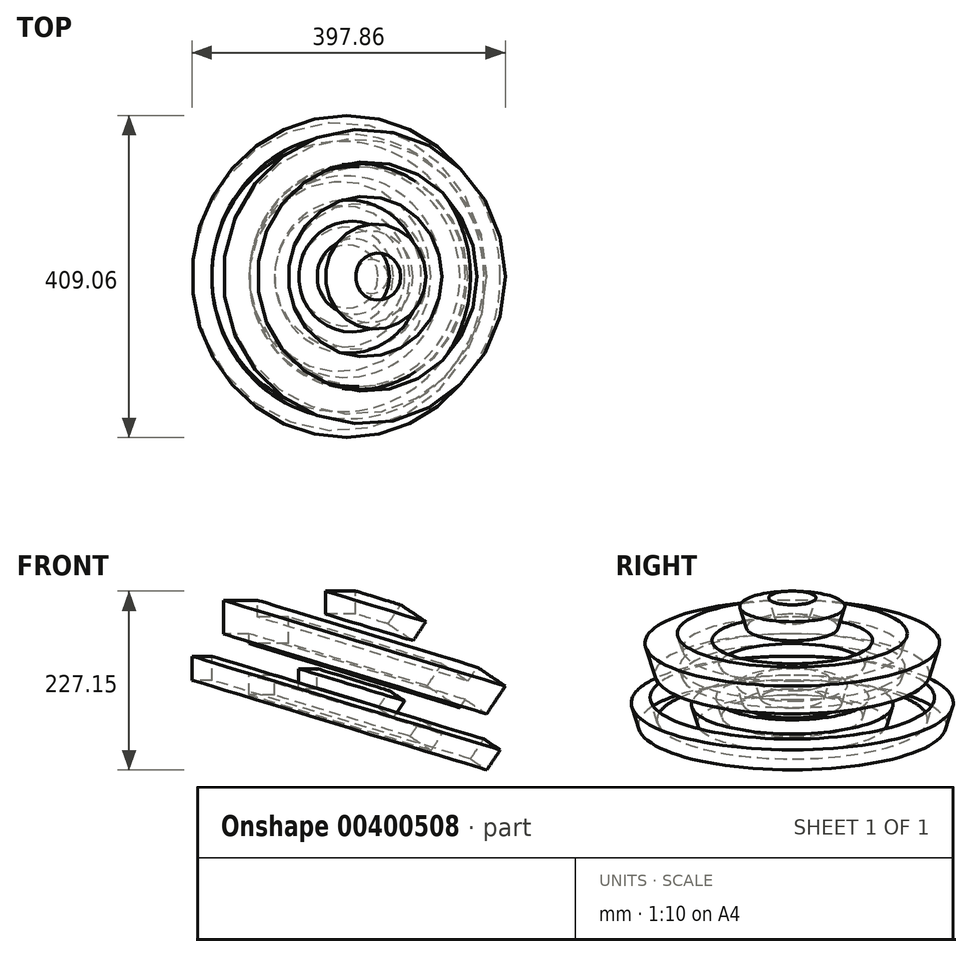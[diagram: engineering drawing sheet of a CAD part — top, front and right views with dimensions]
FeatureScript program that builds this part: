
annotation { "Feature Type Name" : "Feature", "Feature Type Description" : "" }
export const myFeature = defineFeature(function(context is Context, id is Id, definition is map)
    precondition{}
    {
        {
            var Q0;
            Q0=qCreatedBy(makeId("Front.planeOp"),FACE);
            var sketch = newSketch(context, id + "F0", { "sketchPlane" : qUnion([Q0])});
            skLineSegment(sketch, "E0.bottom", {"start": v(-60.63, 55.11) * mm, "end": v(-17.62, 55.11) * mm});
            skLineSegment(sketch, "E0.top", {"start": v(-60.63, 12.54) * mm, "end": v(-17.62, 12.54) * mm});
            skLineSegment(sketch, "E0.left", {"start": v(-60.63, 55.11) * mm, "end": v(-60.63, 12.54) * mm});
            skLineSegment(sketch, "E0.right", {"start": v(-17.62, 55.11) * mm, "end": v(-17.62, 12.54) * mm});
            skLineSegment(sketch, "E1.bottom", {"start": v(-27.97, 33.8) * mm, "end": v(21.85, 33.8) * mm});
            skLineSegment(sketch, "E1.top", {"start": v(-27.97, 0) * mm, "end": v(21.85, 0) * mm});
            skLineSegment(sketch, "E1.left", {"start": v(21.85, 33.8) * mm, "end": v(21.85, 0) * mm});
            skLineSegment(sketch, "E1.right", {"start": v(-27.97, 33.8) * mm, "end": v(-27.97, 0) * mm});
            skLineSegment(sketch, "E2.bottom", {"start": v(-27.85, -40.12) * mm, "end": v(4.23, -40.12) * mm});
            skLineSegment(sketch, "E2.top", {"start": v(-27.85, -65.4) * mm, "end": v(4.23, -65.4) * mm});
            skLineSegment(sketch, "E2.left", {"start": v(-27.85, -40.12) * mm, "end": v(-27.85, -65.4) * mm});
            skLineSegment(sketch, "E2.right", {"start": v(4.23, -40.12) * mm, "end": v(4.23, -65.4) * mm});
            skLineSegment(sketch, "E3.bottom", {"start": v(34.9, -31.87) * mm, "end": v(58.51, -31.87) * mm});
            skLineSegment(sketch, "E3.top", {"start": v(34.9, -57.84) * mm, "end": v(58.51, -57.84) * mm});
            skLineSegment(sketch, "E3.left", {"start": v(34.9, -31.87) * mm, "end": v(34.9, -57.84) * mm});
            skLineSegment(sketch, "E3.right", {"start": v(58.51, -31.87) * mm, "end": v(58.51, -57.84) * mm});
            skLineSegment(sketch, "E4.bottom", {"start": v(-100.46, -15.96) * mm, "end": v(-75.43, -15.96) * mm});
            skLineSegment(sketch, "E4.top", {"start": v(-100.46, -46.45) * mm, "end": v(-75.43, -46.45) * mm});
            skLineSegment(sketch, "E4.left", {"start": v(-100.46, -15.96) * mm, "end": v(-100.46, -46.45) * mm});
            skLineSegment(sketch, "E4.right", {"start": v(-75.43, -15.96) * mm, "end": v(-75.43, -46.45) * mm});
            skLineSegment(sketch, "E5.bottom", {"start": v(68.74, 66.72) * mm, "end": v(107.16, 66.72) * mm});
            skLineSegment(sketch, "E5.top", {"start": v(68.74, 37.63) * mm, "end": v(107.16, 37.63) * mm});
            skLineSegment(sketch, "E5.left", {"start": v(68.74, 66.72) * mm, "end": v(68.74, 37.63) * mm});
            skLineSegment(sketch, "E5.right", {"start": v(107.16, 66.72) * mm, "end": v(107.16, 37.63) * mm});
            skLineSegment(sketch, "E6", {"start": v(131, 42) * mm, "end": v(101.12, -56.1) * mm});
            skSolve(sketch);
        }
        {
            var Q0;
            Q0=makeQuery(id+"F0.imprint","IMPRINT",FACE,{"disambiguationData":[TD([[makeQuery(id+"F0.imprint","IMPRINT",EDGE,{"derivedFrom":sQuery(id+"F0.wireOp",EDGE,"E3.bottom")}),-1.0]])]});
            var Q1;
            Q1=makeQuery(id+"F0.imprint","IMPRINT",FACE,{"disambiguationData":[TD([[makeQuery(id+"F0.imprint","IMPRINT",EDGE,{"derivedFrom":sQuery(id+"F0.wireOp",EDGE,"E5.bottom")}),-1.0]])]});
            var Q2;
            {var subQ0=sQuery(id+"F0.wireOp",EDGE,"E1.top");Q2=makeQuery(id+"F0.imprint","IMPRINT",FACE,{"disambiguationData":[TD([[makeQuery(id+"F0.imprint","IMPRINT",EDGE,{"derivedFrom":subQ0}),1.0]])]});}
            var Q3;
            {var subQ0=sQuery(id+"F0.wireOp",EDGE,"E0.right");var subQ1=sQuery(id+"F0.wireOp",EDGE,"E0.top");var subQ2=makeQuery(id+"F0.imprint","INTERSECT",VERTEX,{"derivedFrom":[subQ1,subQ0]});Q3=makeQuery(id+"F0.imprint","IMPRINT",FACE,{"disambiguationData":[TD([[makeQuery(id+"F0.imprint","IMPRINT",EDGE,{"disambiguationData":[TD([[subQ2,1.0]])],"derivedFrom":subQ1}),1.0]])]});}
            var Q4;
            Q4=makeQuery(id+"F0.imprint","IMPRINT",FACE,{"disambiguationData":[TD([[makeQuery(id+"F0.imprint","IMPRINT",EDGE,{"derivedFrom":sQuery(id+"F0.wireOp",EDGE,"E4.bottom")}),-1.0]])]});
            var Q5;
            Q5=makeQuery(id+"F0.imprint","IMPRINT",FACE,{"disambiguationData":[TD([[makeQuery(id+"F0.imprint","IMPRINT",EDGE,{"derivedFrom":sQuery(id+"F0.wireOp",EDGE,"E2.bottom")}),-1.0]])]});
            var Q6;
            {var subQ1=sQuery(id+"F0.wireOp",EDGE,"E0.bottom");Q6=makeQuery(id+"F0.imprint","IMPRINT",FACE,{"disambiguationData":[TD([[makeQuery(id+"F0.imprint","IMPRINT",EDGE,{"derivedFrom":subQ1}),-1.0]])]});}
            var Q7;
            Q7=sQuery(id+"F0.wireOp",EDGE,"E6");
            revolve(context, id + "F1", {"entities" : qUnion([Q0, Q1, Q2, Q3, Q4, Q5, Q6]), "axis" : qUnion([Q7]), "revolveType" : RevolveType.FULL});
        }
    });
